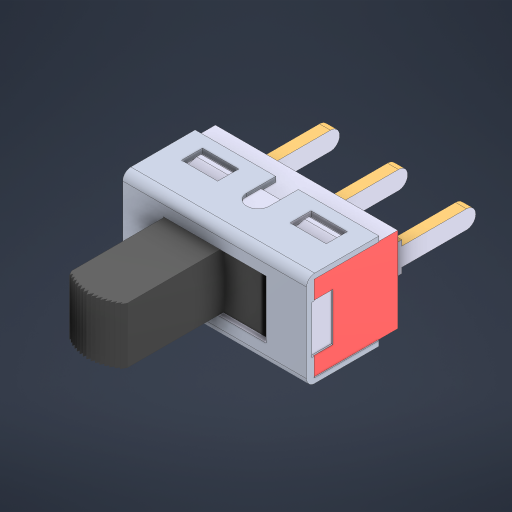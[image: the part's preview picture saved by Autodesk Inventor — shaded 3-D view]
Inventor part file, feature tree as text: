
AUTODESK INVENTOR PART (.ipt)
format: ipt  version: 2024 (Build 280153000, 153)  size: 439,296 bytes
history: native  units: in
note: dims shown in document units (in); Inventor stores cm internally (conversion verified against a paired STEP export)
features: mirror x1
ambient origin geometry x8: Origin, YZ Plane, XZ Plane, XY Plane, X Axis, Y Axis, Z Axis, Center Point
bodies: Solid1 (feature_tree)
feature tree (1):
  mirror  "Mirror1"
